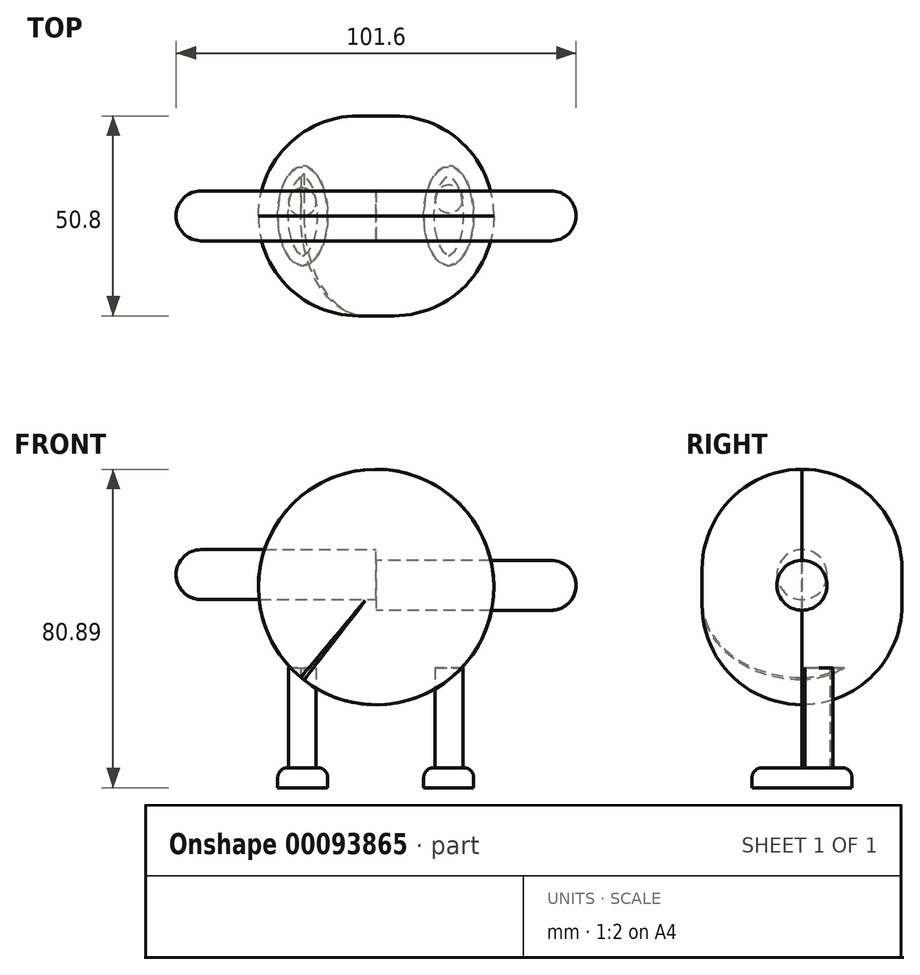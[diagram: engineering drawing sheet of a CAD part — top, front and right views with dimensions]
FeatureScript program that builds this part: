
annotation { "Feature Type Name" : "Feature", "Feature Type Description" : "" }
export const myFeature = defineFeature(function(context is Context, id is Id, definition is map)
    precondition{}
    {
        {
            var Q0;
            Q0=qCreatedBy(makeId("Top.planeOp"),FACE);
            var sketch = newSketch(context, id + "F0", { "sketchPlane" : qUnion([Q0])});
            skLineSegment(sketch, "E0", {"start": v(-18.66, 0) * mm, "end": v(18.43, 0) * mm});
            skEllipse(sketch, "E1", {"center": v(-18.66, 0) * mm, "majorRadius": 12.7 * mm, "minorRadius": 6.35 * mm, "majorAxis": v(0, -1)});
            skEllipse(sketch, "E2", {"center": v(18.43, 0) * mm, "majorRadius": 12.7 * mm, "minorRadius": 6.35 * mm, "majorAxis": v(0, -1)});
            skSolve(sketch);
        }
        {
            var Q0;
            Q0=makeQuery(id+"F0.imprint","IMPRINT",FACE,{"disambiguationData":[TD([[makeQuery(id+"F0.imprint","IMPRINT",EDGE,{"derivedFrom":sQuery(id+"F0.wireOp",EDGE,"E1")}),1.0]])]});
            var Q1;
            Q1=makeQuery(id+"F0.imprint","IMPRINT",FACE,{"disambiguationData":[TD([[makeQuery(id+"F0.imprint","IMPRINT",EDGE,{"derivedFrom":sQuery(id+"F0.wireOp",EDGE,"E2")}),1.0]])]});
            extrude(context, id + "F1", {"entities" : qUnion([Q0, Q1]), "depth" : 5.08 * mm});
        }
        {
            var Q0;
            Q0=makeQuery(id+"F1.opExtrude","CAP_EDGE",EDGE,{"disambiguationData":[OSD([sQuery(id+"F0.wireOp",EDGE,"E1")])],"isStart":false});
            var Q1;
            Q1=makeQuery(id+"F1.opExtrude","CAP_EDGE",EDGE,{"disambiguationData":[OSD([sQuery(id+"F0.wireOp",EDGE,"E2")])],"isStart":false});
            fillet(context, id + "F2", {"entities" : qUnion([Q0, Q1]), "radius" : 2.54 * mm, "tangentPropagation" : true, "allowEdgeOverflow" : false});
        }
        {
            var Q0;
            Q0=makeQuery(id+"F1.opExtrude","CAP_FACE",FACE,{"disambiguationData":[OSD([sQuery(id+"F0.wireOp",EDGE,"E1")])],"isStart":false});
            var sketch = newSketch(context, id + "F3", { "sketchPlane" : qUnion([Q0])});
            skCircle(sketch, "E3", {"center": v(-18.74, 3.5) * mm, "radius": 3.53 * mm});
            skCircle(sketch, "E4", {"center": v(18.5, 4.3) * mm, "radius": 3.53 * mm});
            skSolve(sketch);
        }
        {
            var Q0;
            Q0 = qSketchRegion(id + "F3", true);
            extrude(context, id + "F4", {"entities" : qUnion([Q0]), "depth" : 25.4 * mm});
        }
        {
            var Q0;
            Q0=qCreatedBy(makeId("Front.planeOp"),FACE);
            var sketch = newSketch(context, id + "F5", { "sketchPlane" : qUnion([Q0])});
            skCircle(sketch, "E5", {"center": v(0, 50.98) * mm, "radius": 29.91 * mm});
            skSolve(sketch);
        }
        {
            var Q0;
            Q0 = qSketchRegion(id + "F5", true);
            extrude(context, id + "F6", {"entities" : qUnion([Q0]), "operationType" : NewBodyOperationType.ADD, "depth" : 25.4 * mm});
        }
        {
            var Q0;
            Q0=makeQuery(id+"F6.opExtrude","CAP_FACE",FACE,{"disambiguationData":[OSD([sQuery(id+"F5.wireOp",EDGE,"E5")])],"isStart":true});
            extrude(context, id + "F7", {"entities" : qUnion([Q0]), "depth" : 25.4 * mm});
        }
        {
            var Q0;
            Q0=makeQuery(id+"F7.opExtrude","CAP_EDGE",EDGE,{"disambiguationData":[OSD([sQuery(id+"F5.wireOp",EDGE,"E5")])],"isStart":false});
            var Q1;
            Q1=makeQuery(id+"F6.opExtrude","CAP_EDGE",EDGE,{"disambiguationData":[OSD([sQuery(id+"F5.wireOp",EDGE,"E5")])],"isStart":false});
            fillet(context, id + "F8", {"entities" : qUnion([Q0, Q1]), "radius" : 25.4 * mm, "tangentPropagation" : true, "allowEdgeOverflow" : false});
        }
        {
            var Q0;
            Q0=qCreatedBy(makeId("Right.planeOp"),FACE);
            var sketch = newSketch(context, id + "F9", { "sketchPlane" : qUnion([Q0])});
            skCircle(sketch, "E6", {"center": v(0, 51.42) * mm, "radius": 6.35 * mm});
            skSolve(sketch);
        }
        {
            var Q0;
            Q0 = qSketchRegion(id + "F9", true);
            extrude(context, id + "F10", {"entities" : qUnion([Q0]), "depth" : 50.8 * mm});
        }
        {
            var Q0;
            Q0=makeQuery(id+"F10.opExtrude","CAP_EDGE",EDGE,{"disambiguationData":[OSD([sQuery(id+"F9.wireOp",EDGE,"E6")])],"isStart":false});
            fillet(context, id + "F11", {"entities" : qUnion([Q0]), "radius" : 6.35 * mm, "tangentPropagation" : true, "allowEdgeOverflow" : false});
        }
        {
            var Q0;
            Q0=qCreatedBy(makeId("Right.planeOp"),FACE);
            var sketch = newSketch(context, id + "F12", { "sketchPlane" : qUnion([Q0])});
            skCircle(sketch, "E7", {"center": v(0, 54.13) * mm, "radius": 6.35 * mm});
            skSolve(sketch);
        }
        {
            var Q0;
            Q0 = qSketchRegion(id + "F12", true);
            extrude(context, id + "F13", {"entities" : qUnion([Q0]), "oppositeDirection" : true, "depth" : 50.8 * mm});
        }
        {
            var Q0;
            Q0=makeQuery(id+"F13.opExtrude","CAP_EDGE",EDGE,{"disambiguationData":[OSD([sQuery(id+"F12.wireOp",EDGE,"E7")])],"isStart":false});
            fillet(context, id + "F14", {"entities" : qUnion([Q0]), "radius" : 6.35 * mm, "tangentPropagation" : true, "allowEdgeOverflow" : false});
        }
    });
